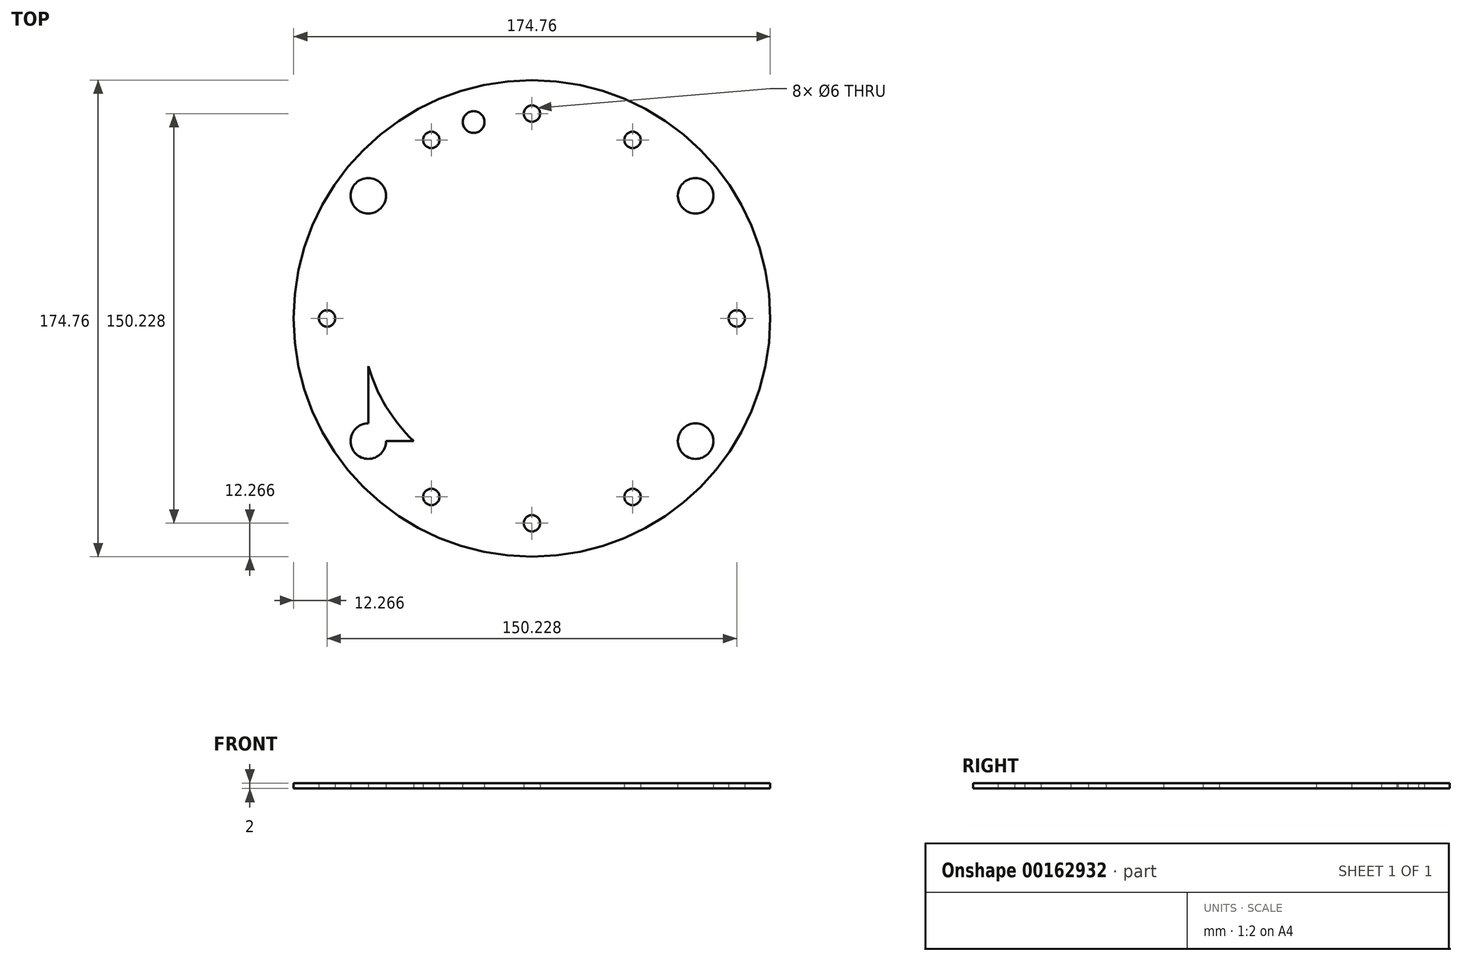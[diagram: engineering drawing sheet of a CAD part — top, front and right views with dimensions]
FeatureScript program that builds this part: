
annotation { "Feature Type Name" : "Feature", "Feature Type Description" : "" }
export const myFeature = defineFeature(function(context is Context, id is Id, definition is map)
    precondition{}
    {
        {
            var Q0;
            Q0=qCreatedBy(makeId("Top.planeOp"),FACE);
            var sketch = newSketch(context, id + "F0", { "sketchPlane" : qUnion([Q0])});
            skLineSegment(sketch, "E0.bottom", {"start": v(60, 45) * mm, "end": v(-60, 45) * mm});
            skLineSegment(sketch, "E0.top", {"start": v(60, -45) * mm, "end": v(-60, -45) * mm});
            skLineSegment(sketch, "E0.left", {"start": v(60, 45) * mm, "end": v(60, -45) * mm});
            skLineSegment(sketch, "E0.right", {"start": v(-60, 45) * mm, "end": v(-60, -45) * mm});
            skPoint(sketch, "E0.middle", {"position": v(0, 0) * mm});
            skCircle(sketch, "E1", {"center": v(60, 45) * mm, "radius": 6.5 * mm});
            skCircle(sketch, "E2", {"center": v(-60, 45) * mm, "radius": 6.5 * mm});
            skCircle(sketch, "E3", {"center": v(60, -45) * mm, "radius": 6.5 * mm});
            skCircle(sketch, "E4", {"center": v(-60, -45) * mm, "radius": 6.5 * mm});
            skCircle(sketch, "E5", {"center": v(0, 0) * mm, "radius": 87.38 * mm});
            skLineSegment(sketch, "E6.bottom", {"start": v(57.9, 51.15) * mm, "end": v(62.1, 51.15) * mm});
            skLineSegment(sketch, "E6.top", {"start": v(57.9, 38.85) * mm, "end": v(62.1, 38.85) * mm});
            skLineSegment(sketch, "E6.left", {"start": v(57.9, 51.15) * mm, "end": v(57.9, 38.85) * mm});
            skLineSegment(sketch, "E6.right", {"start": v(62.1, 51.15) * mm, "end": v(62.1, 38.85) * mm});
            skLineSegment(sketch, "E7.bottom", {"start": v(-62.1, 51.15) * mm, "end": v(-57.9, 51.15) * mm});
            skLineSegment(sketch, "E7.top", {"start": v(-62.1, 38.85) * mm, "end": v(-57.9, 38.85) * mm});
            skLineSegment(sketch, "E7.left", {"start": v(-62.1, 51.15) * mm, "end": v(-62.1, 38.85) * mm});
            skLineSegment(sketch, "E7.right", {"start": v(-57.9, 51.15) * mm, "end": v(-57.9, 38.85) * mm});
            skLineSegment(sketch, "E8.bottom", {"start": v(62.1, -38.85) * mm, "end": v(57.9, -38.85) * mm});
            skLineSegment(sketch, "E8.top", {"start": v(62.1, -51.15) * mm, "end": v(57.9, -51.15) * mm});
            skLineSegment(sketch, "E8.left", {"start": v(62.1, -38.85) * mm, "end": v(62.1, -51.15) * mm});
            skLineSegment(sketch, "E8.right", {"start": v(57.9, -38.85) * mm, "end": v(57.9, -51.15) * mm});
            skLineSegment(sketch, "E9.bottom", {"start": v(-62.1, -38.85) * mm, "end": v(-57.9, -38.85) * mm});
            skLineSegment(sketch, "E9.top", {"start": v(-62.1, -51.15) * mm, "end": v(-57.9, -51.15) * mm});
            skLineSegment(sketch, "E9.left", {"start": v(-62.1, -38.85) * mm, "end": v(-62.1, -51.15) * mm});
            skLineSegment(sketch, "E9.right", {"start": v(-57.9, -38.85) * mm, "end": v(-57.9, -51.15) * mm});
            skLineSegment(sketch, "E10.bottom", {"start": v(57.9, -38.85) * mm, "end": v(80.67, -38.85) * mm});
            skLineSegment(sketch, "E10.top", {"start": v(57.9, -51.15) * mm, "end": v(80.67, -51.15) * mm});
            skLineSegment(sketch, "E10.right", {"start": v(80.67, -38.85) * mm, "end": v(80.67, -51.15) * mm});
            skLineSegment(sketch, "E11.bottom", {"start": v(57.9, 51.15) * mm, "end": v(78.26, 51.15) * mm});
            skLineSegment(sketch, "E11.top", {"start": v(57.9, 38.85) * mm, "end": v(78.26, 38.85) * mm});
            skLineSegment(sketch, "E11.right", {"start": v(78.26, 51.15) * mm, "end": v(78.26, 38.85) * mm});
            skLineSegment(sketch, "E12.bottom", {"start": v(-57.9, 51.15) * mm, "end": v(-78.26, 51.15) * mm});
            skLineSegment(sketch, "E12.top", {"start": v(-57.9, 38.85) * mm, "end": v(-78.26, 38.85) * mm});
            skLineSegment(sketch, "E12.right", {"start": v(-78.26, 51.15) * mm, "end": v(-78.26, 38.85) * mm});
            skLineSegment(sketch, "E13.bottom", {"start": v(-57.9, -38.85) * mm, "end": v(-78.26, -38.85) * mm});
            skLineSegment(sketch, "E13.top", {"start": v(-57.9, -51.15) * mm, "end": v(-78.26, -51.15) * mm});
            skLineSegment(sketch, "E13.right", {"start": v(-78.26, -38.85) * mm, "end": v(-78.26, -51.15) * mm});
            skCircle(sketch, "E14", {"center": v(0, 0) * mm, "radius": 62.5 * mm});
            skCircle(sketch, "E15", {"center": v(0, 75.11) * mm, "radius": 3 * mm});
            skCircle(sketch, "E16", {"center": v(0, -75.11) * mm, "radius": 3 * mm});
            skCircle(sketch, "E17", {"center": v(75.11, 0) * mm, "radius": 3 * mm});
            skCircle(sketch, "E18", {"center": v(-75.11, 0) * mm, "radius": 3 * mm});
            skCircle(sketch, "E19", {"center": v(-21.38, 72.03) * mm, "radius": 4 * mm});
            skCircle(sketch, "E20", {"center": v(0, 0) * mm, "radius": 75.13 * mm});
            skLineSegment(sketch, "E21.bottom", {"start": v(36.9, 65.45) * mm, "end": v(-36.9, 65.45) * mm});
            skLineSegment(sketch, "E21.top", {"start": v(36.9, -65.45) * mm, "end": v(-36.9, -65.45) * mm});
            skLineSegment(sketch, "E21.left", {"start": v(36.9, 65.45) * mm, "end": v(36.9, -65.45) * mm});
            skLineSegment(sketch, "E21.right", {"start": v(-36.9, 65.45) * mm, "end": v(-36.9, -65.45) * mm});
            skCircle(sketch, "E22", {"center": v(-36.9, 65.45) * mm, "radius": 3 * mm});
            skCircle(sketch, "E23", {"center": v(36.9, 65.45) * mm, "radius": 3 * mm});
            skCircle(sketch, "E24", {"center": v(36.9, -65.45) * mm, "radius": 3 * mm});
            skCircle(sketch, "E25", {"center": v(-36.9, -65.45) * mm, "radius": 3 * mm});
            skSolve(sketch);
        }
        {
            var Q0;
            {var subQ0=sQuery(id+"F0.wireOp",EDGE,"E11.bottom");var subQ3=sQuery(id+"F0.wireOp",EDGE,"E5");var subQ4=makeQuery(id+"F0.imprint","INTERSECT",VERTEX,{"derivedFrom":[subQ3,subQ0]});Q0=makeQuery(id+"F0.imprint","IMPRINT",FACE,{"disambiguationData":[TD([[makeQuery(id+"F0.imprint","IMPRINT",EDGE,{"disambiguationData":[TD([[subQ4,-1.0]])],"derivedFrom":subQ3}),1.0]])]});}
            var Q1;
            {var subQ3=sQuery(id+"F0.wireOp",EDGE,"E20");var subQ7=sQuery(id+"F0.wireOp",EDGE,"E2");var subQ9=makeQuery(id+"F0.imprint","INTERSECT",VERTEX,{"disambiguationData":[OD(1.0)],"derivedFrom":[subQ7,subQ3]});Q1=makeQuery(id+"F0.imprint","IMPRINT",FACE,{"disambiguationData":[TD([[makeQuery(id+"F0.imprint","IMPRINT",EDGE,{"disambiguationData":[TD([[subQ9,-1.0]])],"derivedFrom":subQ3}),-1.0]])]});}
            var Q2;
            {var subQ0=sQuery(id+"F0.wireOp",EDGE,"E14");var subQ1=sQuery(id+"F0.wireOp",EDGE,"E0.bottom");var subQ2=makeQuery(id+"F0.imprint","INTERSECT",VERTEX,{"disambiguationData":[OD(1.0)],"derivedFrom":[subQ1,subQ0]});Q2=makeQuery(id+"F0.imprint","IMPRINT",FACE,{"disambiguationData":[TD([[makeQuery(id+"F0.imprint","IMPRINT",EDGE,{"disambiguationData":[TD([[subQ2,-1.0]])],"derivedFrom":subQ1}),-1.0]])]});}
            var Q3;
            {var subQ0=sQuery(id+"F0.wireOp",EDGE,"E21.right");var subQ1=sQuery(id+"F0.wireOp",EDGE,"E0.bottom");var subQ2=makeQuery(id+"F0.imprint","INTERSECT",VERTEX,{"derivedFrom":[subQ1,subQ0]});Q3=makeQuery(id+"F0.imprint","IMPRINT",FACE,{"disambiguationData":[TD([[makeQuery(id+"F0.imprint","IMPRINT",EDGE,{"disambiguationData":[TD([[subQ2,-1.0]])],"derivedFrom":subQ1}),-1.0]])]});}
            var Q4;
            {var subQ1=sQuery(id+"F0.wireOp",EDGE,"E2");var subQ3=sQuery(id+"F0.wireOp",EDGE,"E20");var subQ4=makeQuery(id+"F0.imprint","INTERSECT",VERTEX,{"disambiguationData":[OD(1.0)],"derivedFrom":[subQ1,subQ3]});Q4=makeQuery(id+"F0.imprint","IMPRINT",FACE,{"disambiguationData":[TD([[makeQuery(id+"F0.imprint","IMPRINT",EDGE,{"disambiguationData":[TD([[subQ4,-1.0]])],"derivedFrom":subQ3}),1.0]])]});}
            var Q5;
            {var subQ2=sQuery(id+"F0.wireOp",EDGE,"E0.bottom");var subQ6=sQuery(id+"F0.wireOp",EDGE,"E14");var subQ8=makeQuery(id+"F0.imprint","INTERSECT",VERTEX,{"disambiguationData":[OD(1.0)],"derivedFrom":[subQ2,subQ6]});Q5=makeQuery(id+"F0.imprint","IMPRINT",FACE,{"disambiguationData":[TD([[makeQuery(id+"F0.imprint","IMPRINT",EDGE,{"disambiguationData":[TD([[subQ8,-1.0]])],"derivedFrom":subQ2}),1.0]])]});}
            var Q6;
            {var subQ0=sQuery(id+"F0.wireOp",EDGE,"E21.left");var subQ1=sQuery(id+"F0.wireOp",EDGE,"E14");var subQ2=makeQuery(id+"F0.imprint","INTERSECT",VERTEX,{"disambiguationData":[OD(0.0)],"derivedFrom":[subQ1,subQ0]});Q6=makeQuery(id+"F0.imprint","IMPRINT",FACE,{"disambiguationData":[TD([[makeQuery(id+"F0.imprint","IMPRINT",EDGE,{"disambiguationData":[TD([[subQ2,-1.0]])],"derivedFrom":subQ1}),-1.0]])]});}
            var Q7;
            {var subQ0=sQuery(id+"F0.wireOp",EDGE,"E20");var subQ1=sQuery(id+"F0.wireOp",EDGE,"E15");var subQ5=makeQuery(id+"F0.imprint","INTERSECT",VERTEX,{"disambiguationData":[OD(0.0)],"derivedFrom":[subQ1,subQ0]});Q7=makeQuery(id+"F0.imprint","IMPRINT",FACE,{"disambiguationData":[TD([[makeQuery(id+"F0.imprint","IMPRINT",EDGE,{"disambiguationData":[TD([[subQ5,1.0]])],"derivedFrom":subQ1}),-1.0]])]});}
            var Q8;
            {var subQ1=sQuery(id+"F0.wireOp",EDGE,"E1");var subQ6=sQuery(id+"F0.wireOp",EDGE,"E0.bottom");var subQ10=makeQuery(id+"F0.imprint","INTERSECT",VERTEX,{"derivedFrom":[subQ6,subQ1]});Q8=makeQuery(id+"F0.imprint","IMPRINT",FACE,{"disambiguationData":[TD([[makeQuery(id+"F0.imprint","IMPRINT",EDGE,{"disambiguationData":[TD([[subQ10,-1.0]])],"derivedFrom":subQ6}),-1.0]])]});}
            var Q9;
            {var subQ1=sQuery(id+"F0.wireOp",EDGE,"E0.bottom");var subQ5=sQuery(id+"F0.wireOp",EDGE,"E21.right");var subQ6=makeQuery(id+"F0.imprint","INTERSECT",VERTEX,{"derivedFrom":[subQ1,subQ5]});Q9=makeQuery(id+"F0.imprint","IMPRINT",FACE,{"disambiguationData":[TD([[makeQuery(id+"F0.imprint","IMPRINT",EDGE,{"disambiguationData":[TD([[subQ6,-1.0]])],"derivedFrom":subQ1}),1.0]])]});}
            var Q10;
            {var subQ0=sQuery(id+"F0.wireOp",EDGE,"E21.left");var subQ1=sQuery(id+"F0.wireOp",EDGE,"E0.bottom");var subQ2=makeQuery(id+"F0.imprint","INTERSECT",VERTEX,{"derivedFrom":[subQ1,subQ0]});Q10=makeQuery(id+"F0.imprint","IMPRINT",FACE,{"disambiguationData":[TD([[makeQuery(id+"F0.imprint","IMPRINT",EDGE,{"disambiguationData":[TD([[subQ2,-1.0]])],"derivedFrom":subQ1}),-1.0]])]});}
            var Q11;
            {var subQ0=sQuery(id+"F0.wireOp",EDGE,"E14");var subQ1=sQuery(id+"F0.wireOp",EDGE,"E0.bottom");var subQ2=makeQuery(id+"F0.imprint","INTERSECT",VERTEX,{"disambiguationData":[OD(0.0)],"derivedFrom":[subQ1,subQ0]});Q11=makeQuery(id+"F0.imprint","IMPRINT",FACE,{"disambiguationData":[TD([[makeQuery(id+"F0.imprint","IMPRINT",EDGE,{"disambiguationData":[TD([[subQ2,-1.0]])],"derivedFrom":subQ1}),1.0]])]});}
            var Q12;
            {var subQ0=sQuery(id+"F0.wireOp",EDGE,"E14");var subQ1=sQuery(id+"F0.wireOp",EDGE,"E0.left");var subQ2=makeQuery(id+"F0.imprint","INTERSECT",VERTEX,{"disambiguationData":[OD(0.0)],"derivedFrom":[subQ1,subQ0]});Q12=makeQuery(id+"F0.imprint","IMPRINT",FACE,{"disambiguationData":[TD([[makeQuery(id+"F0.imprint","IMPRINT",EDGE,{"disambiguationData":[TD([[subQ2,-1.0]])],"derivedFrom":subQ1}),1.0]])]});}
            var Q13;
            {var subQ0=sQuery(id+"F0.wireOp",EDGE,"E1");var subQ4=sQuery(id+"F0.wireOp",EDGE,"E0.bottom");var subQ5=makeQuery(id+"F0.imprint","INTERSECT",VERTEX,{"derivedFrom":[subQ4,subQ0]});Q13=makeQuery(id+"F0.imprint","IMPRINT",FACE,{"disambiguationData":[TD([[makeQuery(id+"F0.imprint","IMPRINT",EDGE,{"disambiguationData":[TD([[subQ5,-1.0]])],"derivedFrom":subQ4}),1.0]])]});}
            var Q14;
            {var subQ0=sQuery(id+"F0.wireOp",EDGE,"E14");var subQ1=sQuery(id+"F0.wireOp",EDGE,"E0.bottom");var subQ2=makeQuery(id+"F0.imprint","INTERSECT",VERTEX,{"disambiguationData":[OD(0.0)],"derivedFrom":[subQ1,subQ0]});Q14=makeQuery(id+"F0.imprint","IMPRINT",FACE,{"disambiguationData":[TD([[makeQuery(id+"F0.imprint","IMPRINT",EDGE,{"disambiguationData":[TD([[subQ2,-1.0]])],"derivedFrom":subQ1}),-1.0]])]});}
            var Q15;
            {var subQ3=sQuery(id+"F0.wireOp",EDGE,"E0.right");var subQ5=sQuery(id+"F0.wireOp",EDGE,"E2");var subQ6=makeQuery(id+"F0.imprint","INTERSECT",VERTEX,{"derivedFrom":[subQ3,subQ5]});Q15=makeQuery(id+"F0.imprint","IMPRINT",FACE,{"disambiguationData":[TD([[makeQuery(id+"F0.imprint","IMPRINT",EDGE,{"disambiguationData":[TD([[subQ6,-1.0]])],"derivedFrom":subQ3}),-1.0]])]});}
            var Q16;
            {var subQ0=sQuery(id+"F0.wireOp",EDGE,"E14");var subQ1=sQuery(id+"F0.wireOp",EDGE,"E0.right");var subQ2=makeQuery(id+"F0.imprint","INTERSECT",VERTEX,{"disambiguationData":[OD(0.0)],"derivedFrom":[subQ1,subQ0]});Q16=makeQuery(id+"F0.imprint","IMPRINT",FACE,{"disambiguationData":[TD([[makeQuery(id+"F0.imprint","IMPRINT",EDGE,{"disambiguationData":[TD([[subQ2,-1.0]])],"derivedFrom":subQ1}),-1.0]])]});}
            var Q17;
            {var subQ0=sQuery(id+"F0.wireOp",EDGE,"E13.right");var subQ1=sQuery(id+"F0.wireOp",EDGE,"E13.bottom");var subQ2=makeQuery(id+"F0.imprint","INTERSECT",VERTEX,{"derivedFrom":[subQ1,subQ0]});Q17=makeQuery(id+"F0.imprint","IMPRINT",FACE,{"disambiguationData":[TD([[makeQuery(id+"F0.imprint","IMPRINT",EDGE,{"disambiguationData":[TD([[subQ2,1.0]])],"derivedFrom":subQ1}),-1.0]])]});}
            var Q18;
            {var subQ1=sQuery(id+"F0.wireOp",EDGE,"E1");var subQ7=sQuery(id+"F0.wireOp",EDGE,"E20");var subQ9=makeQuery(id+"F0.imprint","INTERSECT",VERTEX,{"disambiguationData":[OD(1.0)],"derivedFrom":[subQ1,subQ7]});Q18=makeQuery(id+"F0.imprint","IMPRINT",FACE,{"disambiguationData":[TD([[makeQuery(id+"F0.imprint","IMPRINT",EDGE,{"disambiguationData":[TD([[subQ9,1.0]])],"derivedFrom":subQ7}),-1.0]])]});}
            var Q19;
            {var subQ1=sQuery(id+"F0.wireOp",EDGE,"E1");var subQ3=sQuery(id+"F0.wireOp",EDGE,"E20");var subQ4=makeQuery(id+"F0.imprint","INTERSECT",VERTEX,{"disambiguationData":[OD(1.0)],"derivedFrom":[subQ1,subQ3]});Q19=makeQuery(id+"F0.imprint","IMPRINT",FACE,{"disambiguationData":[TD([[makeQuery(id+"F0.imprint","IMPRINT",EDGE,{"disambiguationData":[TD([[subQ4,1.0]])],"derivedFrom":subQ3}),1.0]])]});}
            var Q20;
            {var subQ3=sQuery(id+"F0.wireOp",EDGE,"E0.left");var subQ6=sQuery(id+"F0.wireOp",EDGE,"E1");var subQ8=makeQuery(id+"F0.imprint","INTERSECT",VERTEX,{"derivedFrom":[subQ3,subQ6]});Q20=makeQuery(id+"F0.imprint","IMPRINT",FACE,{"disambiguationData":[TD([[makeQuery(id+"F0.imprint","IMPRINT",EDGE,{"disambiguationData":[TD([[subQ8,-1.0]])],"derivedFrom":subQ3}),1.0]])]});}
            var Q21;
            {var subQ5=sQuery(id+"F0.wireOp",EDGE,"E5");var subQ8=sQuery(id+"F0.wireOp",EDGE,"E10.bottom");var subQ9=makeQuery(id+"F0.imprint","INTERSECT",VERTEX,{"derivedFrom":[subQ5,subQ8]});Q21=makeQuery(id+"F0.imprint","IMPRINT",FACE,{"disambiguationData":[TD([[makeQuery(id+"F0.imprint","IMPRINT",EDGE,{"disambiguationData":[TD([[subQ9,1.0]])],"derivedFrom":subQ8}),1.0]])]});}
            var Q22;
            {var subQ0=sQuery(id+"F0.wireOp",EDGE,"E21.left");var subQ1=sQuery(id+"F0.wireOp",EDGE,"E0.bottom");var subQ2=makeQuery(id+"F0.imprint","INTERSECT",VERTEX,{"derivedFrom":[subQ1,subQ0]});Q22=makeQuery(id+"F0.imprint","IMPRINT",FACE,{"disambiguationData":[TD([[makeQuery(id+"F0.imprint","IMPRINT",EDGE,{"disambiguationData":[TD([[subQ2,-1.0]])],"derivedFrom":subQ1}),1.0]])]});}
            var Q23;
            {var subQ0=sQuery(id+"F0.wireOp",EDGE,"E21.left");var subQ1=sQuery(id+"F0.wireOp",EDGE,"E0.top");var subQ2=makeQuery(id+"F0.imprint","INTERSECT",VERTEX,{"derivedFrom":[subQ1,subQ0]});Q23=makeQuery(id+"F0.imprint","IMPRINT",FACE,{"disambiguationData":[TD([[makeQuery(id+"F0.imprint","IMPRINT",EDGE,{"disambiguationData":[TD([[subQ2,-1.0]])],"derivedFrom":subQ1}),1.0]])]});}
            var Q24;
            {var subQ0=sQuery(id+"F0.wireOp",EDGE,"E14");var subQ1=sQuery(id+"F0.wireOp",EDGE,"E0.top");var subQ2=makeQuery(id+"F0.imprint","INTERSECT",VERTEX,{"disambiguationData":[OD(0.0)],"derivedFrom":[subQ1,subQ0]});Q24=makeQuery(id+"F0.imprint","IMPRINT",FACE,{"disambiguationData":[TD([[makeQuery(id+"F0.imprint","IMPRINT",EDGE,{"disambiguationData":[TD([[subQ2,-1.0]])],"derivedFrom":subQ1}),1.0]])]});}
            var Q25;
            {var subQ0=sQuery(id+"F0.wireOp",EDGE,"E21.right");var subQ1=sQuery(id+"F0.wireOp",EDGE,"E0.top");var subQ2=makeQuery(id+"F0.imprint","INTERSECT",VERTEX,{"derivedFrom":[subQ1,subQ0]});Q25=makeQuery(id+"F0.imprint","IMPRINT",FACE,{"disambiguationData":[TD([[makeQuery(id+"F0.imprint","IMPRINT",EDGE,{"disambiguationData":[TD([[subQ2,-1.0]])],"derivedFrom":subQ1}),1.0]])]});}
            var Q26;
            {var subQ2=sQuery(id+"F0.wireOp",EDGE,"E0.top");var subQ6=sQuery(id+"F0.wireOp",EDGE,"E14");var subQ8=makeQuery(id+"F0.imprint","INTERSECT",VERTEX,{"disambiguationData":[OD(1.0)],"derivedFrom":[subQ2,subQ6]});Q26=makeQuery(id+"F0.imprint","IMPRINT",FACE,{"disambiguationData":[TD([[makeQuery(id+"F0.imprint","IMPRINT",EDGE,{"disambiguationData":[TD([[subQ8,-1.0]])],"derivedFrom":subQ2}),-1.0]])]});}
            var Q27;
            {var subQ1=sQuery(id+"F0.wireOp",EDGE,"E14");var subQ5=sQuery(id+"F0.wireOp",EDGE,"E21.right");var subQ6=makeQuery(id+"F0.imprint","INTERSECT",VERTEX,{"disambiguationData":[OD(1.0)],"derivedFrom":[subQ1,subQ5]});Q27=makeQuery(id+"F0.imprint","IMPRINT",FACE,{"disambiguationData":[TD([[makeQuery(id+"F0.imprint","IMPRINT",EDGE,{"disambiguationData":[TD([[subQ6,-1.0]])],"derivedFrom":subQ1}),-1.0]])]});}
            var Q28;
            {var subQ5=sQuery(id+"F0.wireOp",EDGE,"E20");var subQ7=sQuery(id+"F0.wireOp",EDGE,"E16");var subQ10=makeQuery(id+"F0.imprint","INTERSECT",VERTEX,{"disambiguationData":[OD(0.0)],"derivedFrom":[subQ7,subQ5]});Q28=makeQuery(id+"F0.imprint","IMPRINT",FACE,{"disambiguationData":[TD([[makeQuery(id+"F0.imprint","IMPRINT",EDGE,{"disambiguationData":[TD([[subQ10,1.0]])],"derivedFrom":subQ7}),-1.0]])]});}
            var Q29;
            {var subQ13=sQuery(id+"F0.wireOp",EDGE,"E13.top");var subQ15=sQuery(id+"F0.wireOp",EDGE,"E5");var subQ16=makeQuery(id+"F0.imprint","INTERSECT",VERTEX,{"derivedFrom":[subQ15,subQ13]});Q29=makeQuery(id+"F0.imprint","IMPRINT",FACE,{"disambiguationData":[TD([[makeQuery(id+"F0.imprint","IMPRINT",EDGE,{"disambiguationData":[TD([[subQ16,-1.0]])],"derivedFrom":subQ15}),1.0]])]});}
            var Q30;
            {var subQ1=sQuery(id+"F0.wireOp",EDGE,"E3");var subQ6=sQuery(id+"F0.wireOp",EDGE,"E0.top");var subQ10=makeQuery(id+"F0.imprint","INTERSECT",VERTEX,{"derivedFrom":[subQ6,subQ1]});Q30=makeQuery(id+"F0.imprint","IMPRINT",FACE,{"disambiguationData":[TD([[makeQuery(id+"F0.imprint","IMPRINT",EDGE,{"disambiguationData":[TD([[subQ10,-1.0]])],"derivedFrom":subQ6}),1.0]])]});}
            var Q31;
            {var subQ0=sQuery(id+"F0.wireOp",EDGE,"E3");var subQ2=sQuery(id+"F0.wireOp",EDGE,"E0.top");var subQ3=makeQuery(id+"F0.imprint","INTERSECT",VERTEX,{"derivedFrom":[subQ2,subQ0]});Q31=makeQuery(id+"F0.imprint","IMPRINT",FACE,{"disambiguationData":[TD([[makeQuery(id+"F0.imprint","IMPRINT",EDGE,{"disambiguationData":[TD([[subQ3,-1.0]])],"derivedFrom":subQ2}),-1.0]])]});}
            var Q32;
            {var subQ0=sQuery(id+"F0.wireOp",EDGE,"E14");var subQ1=sQuery(id+"F0.wireOp",EDGE,"E0.top");var subQ2=makeQuery(id+"F0.imprint","INTERSECT",VERTEX,{"disambiguationData":[OD(1.0)],"derivedFrom":[subQ1,subQ0]});Q32=makeQuery(id+"F0.imprint","IMPRINT",FACE,{"disambiguationData":[TD([[makeQuery(id+"F0.imprint","IMPRINT",EDGE,{"disambiguationData":[TD([[subQ2,-1.0]])],"derivedFrom":subQ1}),1.0]])]});}
            var Q33;
            {var subQ0=sQuery(id+"F0.wireOp",EDGE,"E10.top");var subQ3=sQuery(id+"F0.wireOp",EDGE,"E5");var subQ4=makeQuery(id+"F0.imprint","INTERSECT",VERTEX,{"derivedFrom":[subQ3,subQ0]});Q33=makeQuery(id+"F0.imprint","IMPRINT",FACE,{"disambiguationData":[TD([[makeQuery(id+"F0.imprint","IMPRINT",EDGE,{"disambiguationData":[TD([[subQ4,-1.0]])],"derivedFrom":subQ3}),1.0]])]});}
            var Q34;
            {var subQ1=sQuery(id+"F0.wireOp",EDGE,"E3");var subQ3=sQuery(id+"F0.wireOp",EDGE,"E20");var subQ4=makeQuery(id+"F0.imprint","INTERSECT",VERTEX,{"disambiguationData":[OD(0.0)],"derivedFrom":[subQ1,subQ3]});Q34=makeQuery(id+"F0.imprint","IMPRINT",FACE,{"disambiguationData":[TD([[makeQuery(id+"F0.imprint","IMPRINT",EDGE,{"disambiguationData":[TD([[subQ4,-1.0]])],"derivedFrom":subQ3}),1.0]])]});}
            var Q35;
            {var subQ3=sQuery(id+"F0.wireOp",EDGE,"E5");var subQ5=sQuery(id+"F0.wireOp",EDGE,"E13.right");var subQ6=makeQuery(id+"F0.imprint","INTERSECT",VERTEX,{"derivedFrom":[subQ3,subQ5]});Q35=makeQuery(id+"F0.imprint","IMPRINT",FACE,{"disambiguationData":[TD([[makeQuery(id+"F0.imprint","IMPRINT",EDGE,{"disambiguationData":[TD([[subQ6,-1.0]])],"derivedFrom":subQ3}),1.0]])]});}
            var Q36;
            {var subQ1=sQuery(id+"F0.wireOp",EDGE,"E4");var subQ3=sQuery(id+"F0.wireOp",EDGE,"E20");var subQ4=makeQuery(id+"F0.imprint","INTERSECT",VERTEX,{"disambiguationData":[OD(0.0)],"derivedFrom":[subQ1,subQ3]});Q36=makeQuery(id+"F0.imprint","IMPRINT",FACE,{"disambiguationData":[TD([[makeQuery(id+"F0.imprint","IMPRINT",EDGE,{"disambiguationData":[TD([[subQ4,1.0]])],"derivedFrom":subQ3}),1.0]])]});}
            extrude(context, id + "F1", {"entities" : qUnion([Q0, Q1, Q2, Q3, Q4, Q5, Q6, Q7, Q8, Q9, Q10, Q11, Q12, Q13, Q14, Q15, Q16, Q17, Q18, Q19, Q20, Q21, Q22, Q23, Q24, Q25, Q26, Q27, Q28, Q29, Q30, Q31, Q32, Q33, Q34, Q35, Q36]), "depth" : 2 * mm});
        }
    });
